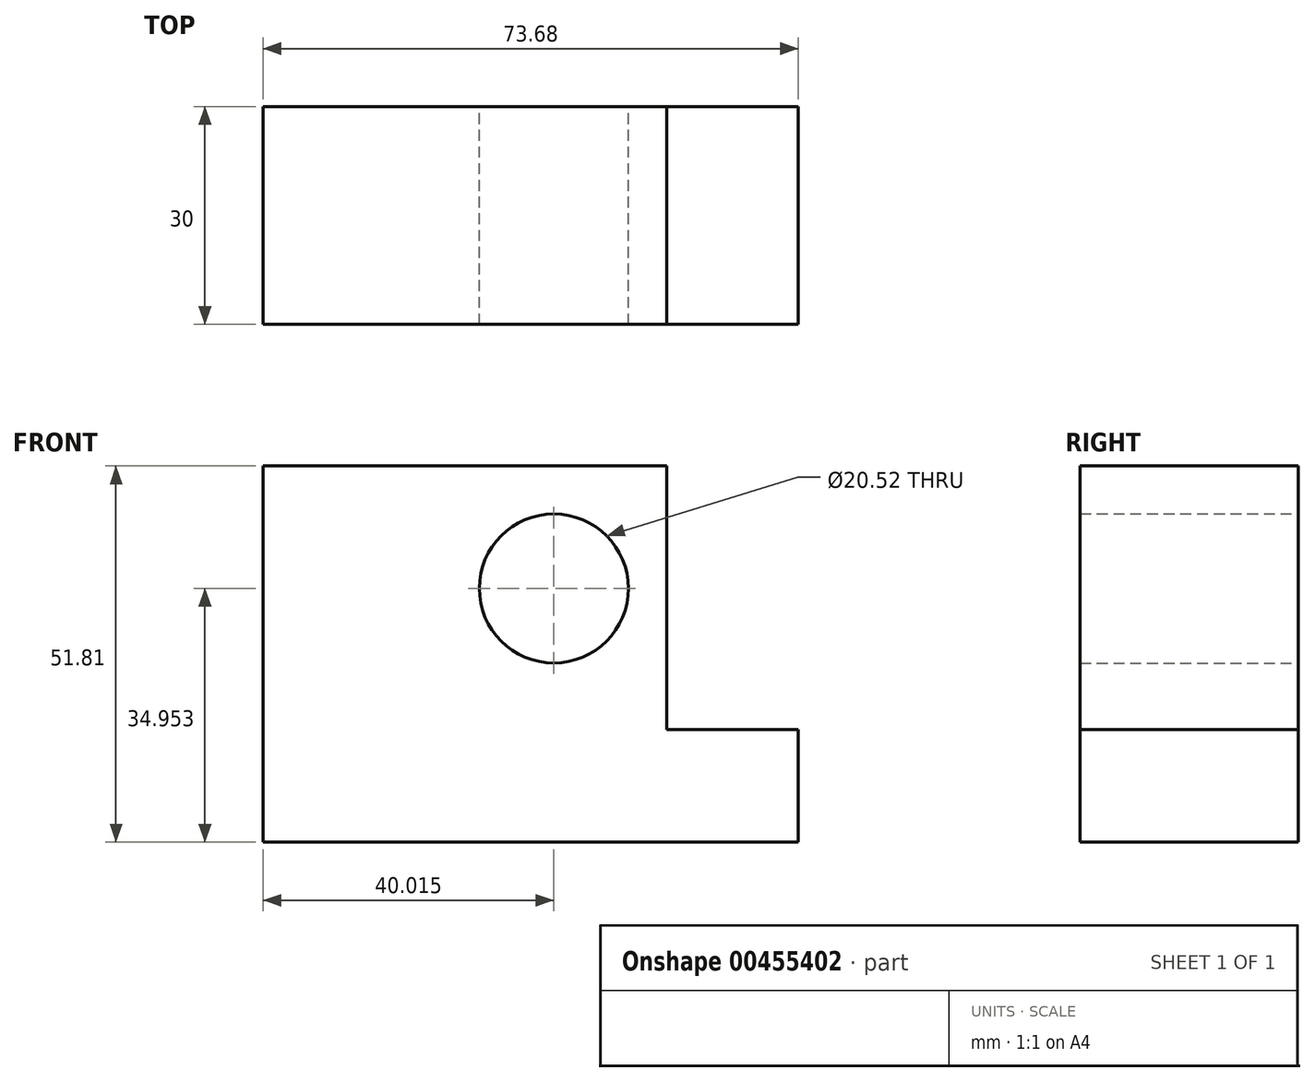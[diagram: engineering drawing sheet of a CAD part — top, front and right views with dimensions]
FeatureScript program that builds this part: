
annotation { "Feature Type Name" : "Feature", "Feature Type Description" : "" }
export const myFeature = defineFeature(function(context is Context, id is Id, definition is map)
    precondition{}
    {
        {
            var Q0;
            Q0=qCreatedBy(makeId("Front.planeOp"),FACE);
            var sketch = newSketch(context, id + "F0", { "sketchPlane" : qUnion([Q0])});
            skLineSegment(sketch, "E0.bottom", {"start": v(-25.9, 25.04) * mm, "end": v(29.64, 25.04) * mm});
            skLineSegment(sketch, "E0.top", {"start": v(-25.9, -26.77) * mm, "end": v(29.64, -26.77) * mm});
            skLineSegment(sketch, "E0.left", {"start": v(-25.9, 25.04) * mm, "end": v(-25.9, -26.77) * mm});
            skLineSegment(sketch, "E0.right", {"start": v(29.64, 25.04) * mm, "end": v(29.64, -11.22) * mm});
            skLineSegment(sketch, "E1.bottom", {"start": v(29.64, -26.77) * mm, "end": v(47.78, -26.77) * mm});
            skLineSegment(sketch, "E1.top", {"start": v(29.64, -11.22) * mm, "end": v(47.78, -11.22) * mm});
            skLineSegment(sketch, "E1.right", {"start": v(47.78, -26.77) * mm, "end": v(47.78, -11.22) * mm});
            skSolve(sketch);
        }
        {
            var Q0;
            Q0=makeQuery(id+"F0.imprint","IMPRINT",FACE,{"disambiguationData":[TD([[makeQuery(id+"F0.imprint","IMPRINT",EDGE,{"derivedFrom":sQuery(id+"F0.wireOp",EDGE,"E0.bottom")}),-1.0]])]});
            extrude(context, id + "F1", {"entities" : qUnion([Q0]), "depth" : 30 * mm});
        }
        {
            var Q0;
            Q0=makeQuery(id+"F1.opExtrude","CAP_FACE",FACE,{"disambiguationData":[OSD([sQuery(id+"F0.wireOp",EDGE,"E0.bottom"),sQuery(id+"F0.wireOp",EDGE,"E0.top"),sQuery(id+"F0.wireOp",EDGE,"E0.left"),sQuery(id+"F0.wireOp",EDGE,"E0.right"),sQuery(id+"F0.wireOp",EDGE,"E1.bottom"),sQuery(id+"F0.wireOp",EDGE,"E1.top"),sQuery(id+"F0.wireOp",EDGE,"E1.right")])],"isStart":true});
            var sketch = newSketch(context, id + "F2", { "sketchPlane" : qUnion([Q0])});
            skCircle(sketch, "E2", {"center": v(-14.12, 8.18) * mm, "radius": 10.26 * mm});
            skSolve(sketch);
        }
        {
            var Q0;
            Q0=makeQuery(id+"F2.imprint","IMPRINT",FACE,{"disambiguationData":[TD([[makeQuery(id+"F2.imprint","IMPRINT",EDGE,{"derivedFrom":sQuery(id+"F2.wireOp",EDGE,"E2")}),1.0]])]});
            extrude(context, id + "F3", {"entities" : qUnion([Q0]), "operationType" : NewBodyOperationType.REMOVE, "oppositeDirection" : true, "depth" : 30 * mm});
        }
    });
